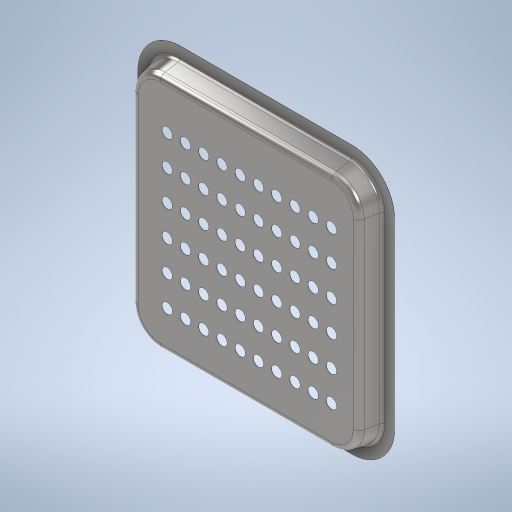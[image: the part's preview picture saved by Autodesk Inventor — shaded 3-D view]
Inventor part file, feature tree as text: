
AUTODESK INVENTOR PART (.ipt)
format: ipt  version: 2024 (Build 280153000, 153)  size: 475,648 bytes
history: native  units: mm
features: projected_geometry x6, other x5, sketch x4, mirror x2, revolve x1, extrude x1, plane x1, pattern_linear x1
ambient origin geometry x8: Origin, YZ Plane, XZ Plane, XY Plane, X Axis, Y Axis, Z Axis, Center Point
bodies: Body1 (feature_tree)
feature tree (21):
  other  "Konturlasche4"
  revolve  "Umdrehung1"
  extrude  "Extrusion1"  Depth=20.0mm
  plane  "Arbeitsebene4"
  mirror  "Spiegeln3"
  mirror  "Spiegeln4"
  pattern_linear  "Rechteckige Anordnung1"  Spacing1=5.0mm  [1 undecoded]
  sketch  "Skizze1"  dims[d4=17.453293mm d5=20.0mm]
  other  "Grobblech5"
  other  "Biegung5"
  other  "Ecke5"
  sketch  "Skizze6"  dims[d6=185.0mm]
  projected_geometry  "Projizierte Kontur1"
  projected_geometry  "Projizierte Kontur2"
  projected_geometry  "Projizierte Kontur3"
  projected_geometry  "Projizierte Kontur4"
  projected_geometry  "Projizierte Kontur5"
  sketch  "Skizze8"  dims[d8=33.5mm]
  sketch  "Skizze9"  dims[d9=10.0mm d10=5.0mm d61=0.35mm d62=0.35mm d63=0.175mm d64=0.7mm d65=0.35mm d66=150.0mm d67=0.35mm d68=0.35mm d69=1.4mm d70=0.35mm d71=0.35mm d75=90.0deg d76=70.0mm d77=10.0mm d78=0.0mm d79=-75.0mm d80=17.0mm d81=55.0mm d82=0.35mm d83=0.0mm d84=60.0mm d86=50.0mm d87=100.0mm d89=30.0mm]
  projected_geometry  "Projizierte Kontur6"
  other  "Ausschneiden1"
note: 1 required parameter value undecoded (feature->parameter linkage not recoverable at this tier; creation-order binding heuristic only, values carry confidence <= 0.55)
